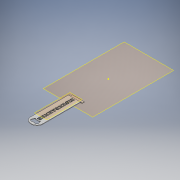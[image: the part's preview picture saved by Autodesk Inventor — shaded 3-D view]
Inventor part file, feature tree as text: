
AUTODESK INVENTOR PART (.ipt)
format: ipt  version: 2018 (Build 220112000, 112)  size: 1,901,056 bytes
history: native  units: mm
features: other x15, sketch x6, plane x2, extrude x1, reference x1, projected_geometry x1
ambient origin geometry x8: Origin, YZ Plane, XZ Plane, XY Plane, X Axis, Y Axis, Z Axis, Center Point
bodies: Volumenkörper1 (feature_tree)
feature tree (26):
  plane  "Arbeitsebene1"
  other  "Fläche1"
  other  "Lasche1"
  other  "Lasche2"
  sketch  "Skizze7"  dims[d9=4.0mm]
  plane  "Arbeitsebene2"
  extrude  "Extrusion3"  Depth=20.0mm
  sketch  "Skizze1"  dims[d3=1.0mm d5=20.0mm]
  reference  "Referenz1"
  other  "Grobblech1"
  sketch  "Skizze2"  dims[d6=2.0mm]
  other  "Grobblech2"
  other  "Biegung1"
  other  "Ecke1"
  sketch  "Skizze3"  dims[d7=2.0mm]
  other  "Grobblech3"
  other  "Biegung2"
  other  "Ecke2"
  sketch  "Skizze5"  dims[d8=1.0mm]
  projected_geometry  "Projizierte Kontur1"
  sketch  "Skizze8"  dims[d10=2.0mm d11=8.05mm d12=90.0deg d13=2.0mm d14=8.0mm d15=2.0mm d16=2.0mm d17=2.0mm d18=1.0mm d19=4.0mm d20=2.0mm d21=12.0mm d22=90.0deg d23=2.0mm d24=8.0mm d25=2.0mm d26=2.0mm d125=2.0mm d126=0.0mm d135=5.0mm d136=10.0mm d137=0.0mm]
  other  "Ausklinkung1"
  other  "<userpath>\AppData\Local\Autodesk\Autodesk Sync\Cloud\jr9343s\Rost_Basis.iam"
  other  "Rost_Basis.iam"
  other  "Volumenkörper1:1"
  other  "Definition1"
